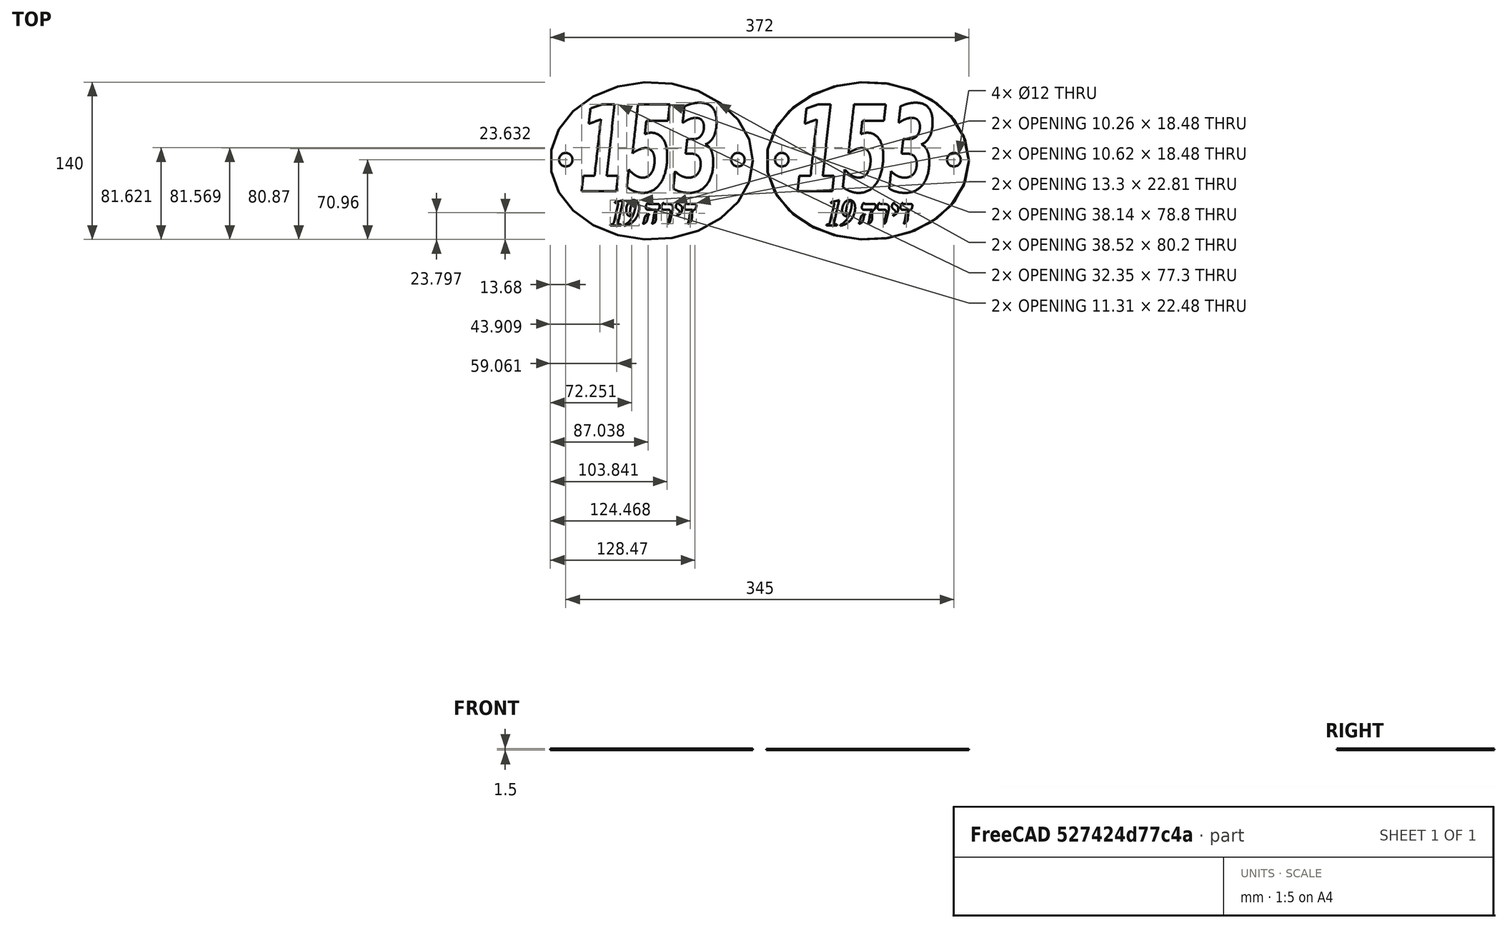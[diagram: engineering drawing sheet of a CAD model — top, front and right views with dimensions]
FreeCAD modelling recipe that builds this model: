
FCSTD DOCUMENT  (FreeCAD 0.18R16110 (Git))
Label: placa_janaya
License: All rights reserved
LicenseURL: http://en.wikipedia.org/wiki/All_rights_reserved
objects: Part::Cut×16, Part::Feature×14, Part::Extrusion×12, Part::Cylinder×2, Part::Part2DObjectPython×1, Part::Box×1
note: 46 computed .brp shape members not serialized (recipe doc carries the construction recipe); baked Part::Feature solids carry a one-line shape summary decoded from their .brp

FEATURE [Part::Feature] path819
  shape: bbox 32.35 x 77.3 x 2.649e-07 mm, 0 faces, 0 solids (baked)
FEATURE [Part::Feature] path821
  shape: bbox 38.14 x 78.8 x 2.649e-07 mm, 0 faces, 0 solids (baked)
FEATURE [Part::Feature] path823
  shape: bbox 38.52 x 80.2 x 2.649e-07 mm, 0 faces, 0 solids (baked)
FEATURE [Part::Extrusion] Extrude_path819  label="1_janaya"
  Base = -> path819
  Dir = (0,0,10)
  DirMode = 0
  FaceMakerClass = Part::FaceMakerExtrusion
  LengthFwd = 0
  LengthRev = 0
  Placement = pos=(0,0,-20) rot=(0,0,1;0rad)
  Solid = true
  Symmetric = false
FEATURE [Part::Extrusion] Extrude_path821  label="5_janaya"
  Base = -> path821
  Dir = (0,0,10)
  DirMode = 0
  FaceMakerClass = Part::FaceMakerExtrusion
  LengthFwd = 0
  LengthRev = 0
  Placement = pos=(0,0,-20) rot=(0,0,1;0rad)
  Solid = true
  Symmetric = false
FEATURE [Part::Extrusion] Extrude_path823  label="3_janaya"
  Base = -> path823
  Dir = (0,0,10)
  DirMode = 0
  FaceMakerClass = Part::FaceMakerExtrusion
  LengthFwd = 0
  LengthRev = 0
  Placement = pos=(0,0,-20) rot=(0,0,1;0rad)
  Solid = true
  Symmetric = false
FEATURE [Part::Part2DObjectPython] Ellipse  # Draft 2D object (typed FeaturePython)
  FirstAngle = 0
  LastAngle = 0
  MajorRadius = 90
  MakeFace = true
  MinorRadius = 70
  Placement = pos=(60.32,-53.96,0) rot=(0,0,1;0rad)
FEATURE [Part::Feature] path2029001
  shape: bbox 5.508 x 8.42 x 2.195e-07 mm, 0 faces, 0 solids (baked)
FEATURE [Part::Feature] path2023
  shape: bbox 10.62 x 18.48 x 2.195e-07 mm, 0 faces, 0 solids (baked)
FEATURE [Part::Feature] path2021
  shape: bbox 13.3 x 22.81 x 2.195e-07 mm, 0 faces, 0 solids (baked)
FEATURE [Part::Extrusion] Extrude001  label="nueve_maciso"
  Base = -> path2021
  Dir = (0,0,1)
  DirMode = 2
  FaceMakerClass = Part::FaceMakerBullseye
  LengthFwd = 10
  LengthRev = 0
  Placement = pos=(0,0,-10) rot=(0,0,1;0rad)
  Solid = true
  Symmetric = false
FEATURE [Part::Feature] path2021001
  shape: bbox 5.081 x 11.95 x 2.195e-07 mm, 0 faces, 0 solids (baked)
FEATURE [Part::Feature] path2029
  shape: bbox 12.35 x 18.48 x 2.195e-07 mm, 0 faces, 0 solids (baked)
FEATURE [Part::Feature] path2019
  shape: bbox 11.31 x 22.48 x 2.195e-07 mm, 0 faces, 0 solids (baked)
FEATURE [Part::Feature] path2025
  shape: bbox 5.655 x 11.62 x 2.195e-07 mm, 0 faces, 0 solids (baked)
FEATURE [Part::Feature] path2027
  shape: bbox 10.26 x 18.48 x 2.195e-07 mm, 0 faces, 0 solids (baked)
FEATURE [Part::Extrusion] Extrude  label="uno"
  Base = -> path2019
  Dir = (0,0,1)
  DirMode = 2
  FaceMakerClass = Part::FaceMakerBullseye
  LengthFwd = 10
  LengthRev = 0
  Placement = pos=(26,-85,-20) rot=(0,0,1;0rad)
  Solid = true
  Symmetric = false
FEATURE [Part::Extrusion] Extrude002  label="nueve_interno"
  Base = -> path2021001
  Dir = (0,0,-1)
  DirMode = 2
  FaceMakerClass = Part::FaceMakerBullseye
  LengthFwd = 10
  LengthRev = 0
  Solid = true
  Symmetric = false
FEATURE [Part::Extrusion] Extrude005  label="reish"
  Base = -> path2027
  Dir = (0,0,-1)
  DirMode = 2
  FaceMakerClass = Part::FaceMakerBullseye
  LengthFwd = 10
  LengthRev = 0
  Placement = pos=(21,-83,-10) rot=(0,0,1;0rad)
  Solid = true
  Symmetric = false
FEATURE [Part::Extrusion] Extrude003  label="dalet"
  Base = -> path2023
  Dir = (0,0,-1)
  DirMode = 2
  FaceMakerClass = Part::FaceMakerBullseye
  LengthFwd = 10
  LengthRev = 0
  Placement = pos=(21,-83,-10) rot=(0,0,1;0rad)
  Solid = true
  Symmetric = false
FEATURE [Part::Extrusion] Extrude004  label="yud"
  Base = -> path2025
  Dir = (0,0,-1)
  DirMode = 2
  FaceMakerClass = Part::FaceMakerBullseye
  LengthFwd = 10
  LengthRev = 0
  Placement = pos=(21,-83,-10) rot=(0,0,1;0rad)
  Solid = true
  Symmetric = false
FEATURE [Part::Extrusion] Extrude006  label="hey-1"
  Base = -> path2029
  Dir = (0,0,-1)
  DirMode = 2
  FaceMakerClass = Part::FaceMakerBullseye
  LengthFwd = 10
  LengthRev = 0
  Placement = pos=(21,-83,-10) rot=(0,0,1;0rad)
  Solid = true
  Symmetric = false
FEATURE [Part::Extrusion] Extrude015  label="hey-2"
  Base = -> path2029001
  Dir = (0,0,-1)
  DirMode = 2
  FaceMakerClass = Part::FaceMakerBullseye
  LengthFwd = 10
  LengthRev = 0
  Placement = pos=(21,-83,-10) rot=(0,0,1;0rad)
  Solid = true
  Symmetric = false
FEATURE [Part::Feature] Cut001001  label="Cut002"
  Placement = pos=(-57.761,-21.7429,0) rot=(0,0,1;0.610865rad)
  shape: bbox 1.943 x 5.366 x 10 mm, 8 faces (baked)
FEATURE [Part::Feature] Cut001002  label="Cut003"
  Placement = pos=(-56.0036,-31.9817,0) rot=(0,0,1;0.750492rad)
  shape: bbox 1.968 x 5.453 x 10 mm, 8 faces (baked)
FEATURE [Part::Cut] Cut  label="nueve"
  Base = -> Extrude001
  Tool = -> Extrude002
FEATURE [Part::Cut] Cut001003
  Base = -> Cut
  Tool = -> Cut001001
FEATURE [Part::Cut] Cut001004  label="nueve-con-corte"
  Base = -> Cut001003
  Placement = pos=(25,-85,-10) rot=(0,0,1;0rad)
  Tool = -> Cut001002
FEATURE [Part::Extrusion] Extrude017  label="elipse"
  Base = -> Ellipse
  Dir = (0,0,1)
  DirMode = 2
  FaceMakerClass = Part::FaceMakerBullseye
  LengthFwd = 1.5
  LengthRev = 0
  Placement = pos=(6,0,-16) rot=(0,0,1;0rad)
  Solid = true
  Symmetric = false
FEATURE [Part::Cylinder] Cylinder
  Angle = 360
  AttacherType = Attacher::AttachEngine3D
  Height = 10
  Placement = pos=(-10,-53,-20) rot=(0,0,1;0rad)
  Radius = 6
FEATURE [Part::Cylinder] Cylinder001
  Angle = 360
  AttacherType = Attacher::AttachEngine3D
  Height = 10
  Placement = pos=(143,-53,-20) rot=(0,0,1;0rad)
  Radius = 6
FEATURE [Part::Cut] Cut001005
  Base = -> Extrude017
  Tool = -> Cylinder
FEATURE [Part::Cut] Cut001006
  Base = -> Cut001005
  Tool = -> Cylinder001
FEATURE [Part::Cut] Cut001007
  Base = -> Cut001006
  Tool = -> Extrude_path819
FEATURE [Part::Cut] Cut001008
  Base = -> Cut001007
  Tool = -> Extrude_path821
FEATURE [Part::Cut] Cut001009
  Base = -> Cut001008
  Tool = -> Extrude_path823
FEATURE [Part::Cut] Cut001010
  Base = -> Cut001009
  Tool = -> Extrude003
FEATURE [Part::Cut] Cut001011
  Base = -> Cut001010
  Tool = -> Extrude004
FEATURE [Part::Cut] Cut001012
  Base = -> Cut001011
  Tool = -> Extrude005
FEATURE [Part::Cut] Cut001013
  Base = -> Cut001012
  Tool = -> Extrude006
FEATURE [Part::Cut] Cut001014
  Base = -> Cut001013
  Tool = -> Extrude015
FEATURE [Part::Cut] Cut001015
  Base = -> Cut001014
  Tool = -> Extrude
FEATURE [Part::Cut] Cut001016  label="placa_1_5mm"
  Base = -> Cut001015
  Tool = -> Cut001004
FEATURE [Part::Feature] Cut001016001  label="placa_1_5mm001"
  shape: bbox 180 x 140 x 1.5 mm, 184 faces (baked)
FEATURE [Part::Box] Box  label="Cube"
  AttacherType = Attacher::AttachEngine3D
  Height = 10
  Length = 200
  Placement = pos=(-35,-131,-15) rot=(0,0,1;0rad)
  Width = 200
FEATURE [Part::Cut] Cut001016002  label="placa_1mm"
  Base = -> Cut001016001
  Placement = pos=(192,0,0) rot=(0,0,1;0rad)
  Tool = -> Box
